# Revit family: Medical_All_Hill-Rom_The-MetaNeb-System
name_source: partatom
category: Specialty Equipment
revit_build: Autodesk Revit Architecture 2015 (Build: 20140606_1530(x64)
units: mm (PartAtom-declared; Revit-internal decimal feet)

## types (1)
- Default
    Ambient Temperature = 10 to 35 C
    BIMobject category = All
    BIMobject category code = medical-all
    BIMobject main category = Medical
    BIMobject main category code = medical
    Brand url = https://construction.hill-rom.com
    Default Elevation = 4' - 0"
    Depth = 0' - 4"
    Description = The MetaNeb® System combines lung expansion, secretion clearance, and aerosol delivery into a single integrated therapy session—without having to switch between different devices.
    Design country = United States
    Edition number = 1
    Glass material = Glass-Hill-Rom-Display
    Height = 4' - 2 19/32"
    IFC Classification = Furniture
    Installation instructions = https://construction.hill-rom.com
    Manufacturer = Hill-Rom
    Manufacturer country = United States
    Manufacturer name = Hill-Rom
    Masterformat 2014 Code = 11 70 00
    Masterformat 2014 Description = Healthcare Equipment
    Model = The MetaNeb® System
    NBS Reference Code = 75-50
    NBS Reference Description = Medical Safety Systems
    Nominal height = 0' - 0"
    Nominal width = 0' - 0"
    OmniClass Code = 23-25 00 00
    OmniClass Description = Medical and Laboratory Equipment
    Product Guid = 5716cccd-65a8-4325-bc66-1f9b2ef7ba8d
    Product SKU = Hill-Rom-Metaneb
    Product certification = https://www.hill-rom.com
    Product data url = https://bimobject.com
    Product family = Respiratory
    Product group = Metaneb
    Product url = https://respiratorycare.hill-rom.com
    QR code = http://bimobject.com
    Relative humidity = 10% to 95%
    Shell material = Plastic-Hill-Rom-White
    Shell material bottom = Plastic-Hill-Rom-Blue
    Stand material = Steel- Hill-Rom-Stainless
    Switches material = Plastic-Hill-Rom-Light Blue
    Technical description = https://construction.hill-rom.com
    UNSPSC Code = 56
    URL = https://www.hill-rom.com
    Uniclass 1.4 Code = L852
    Uniclass 1.4 Description = Medical furniture, fittings
    Uniclass 2.0 Code = SS-75-50
    Uniclass 2.0 Description = Medical Safety Systems
    Uniclass 2015 Code = Pr_40_70_51
    Uniclass 2015 Name = Medical and laboratory equipment
    Weight = 16.60 lbm
    Wheels material = Plastic-Hill-Rom-Light Blue
    Width = 1' - 3"
    Youtube clip = https://respiratorycare.hill-rom.com

## geometry (parser evidence)
native form markers: Blend x10, Sweep x1
no freeform markers — native parametric forms only
